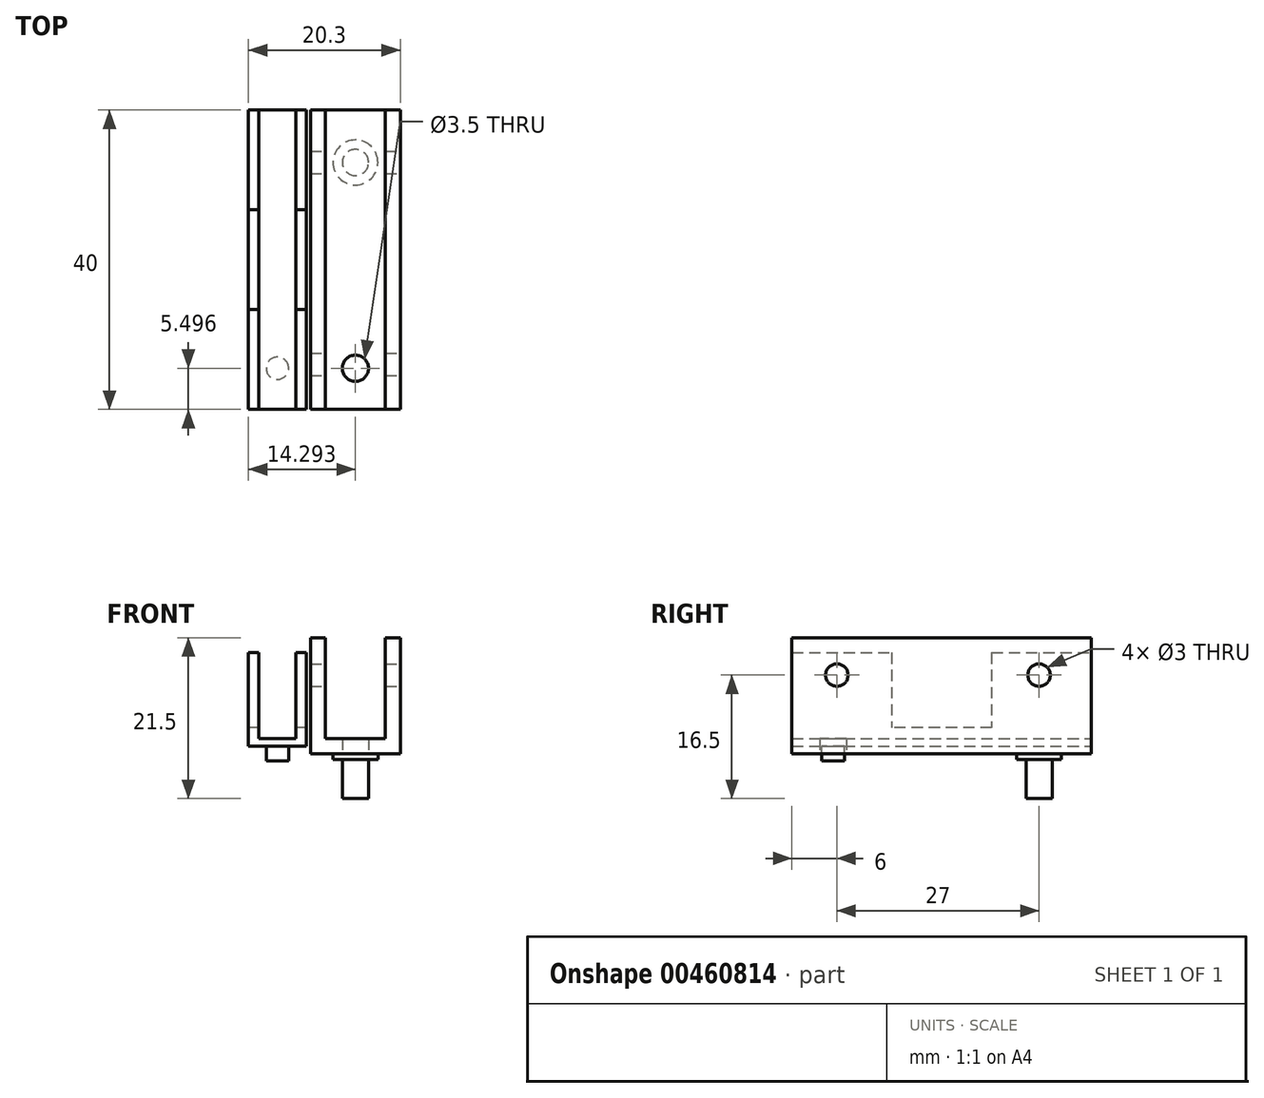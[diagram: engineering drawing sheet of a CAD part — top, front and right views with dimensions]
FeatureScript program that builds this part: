
annotation { "Feature Type Name" : "Feature", "Feature Type Description" : "" }
export const myFeature = defineFeature(function(context is Context, id is Id, definition is map)
    precondition{}
    {
        {
            var Q0;
            Q0=qCreatedBy(makeId("Front.planeOp"),FACE);
            var sketch = newSketch(context, id + "F0", { "sketchPlane" : qUnion([Q0])});
            skLineSegment(sketch, "E0", {"start": v(1.58, 13.5) * mm, "end": v(1.58, 0) * mm});
            skLineSegment(sketch, "E1", {"start": v(1.58, 0) * mm, "end": v(9.58, 0) * mm});
            skLineSegment(sketch, "E2", {"start": v(9.58, 0) * mm, "end": v(9.58, 13.5) * mm});
            skLineSegment(sketch, "E3", {"start": v(9.58, 13.5) * mm, "end": v(11.58, 13.5) * mm});
            skLineSegment(sketch, "E4", {"start": v(11.58, 13.5) * mm, "end": v(11.58, -2) * mm});
            skLineSegment(sketch, "E5", {"start": v(11.58, -2) * mm, "end": v(-0.42, -2) * mm});
            skLineSegment(sketch, "E6", {"start": v(-0.42, -2) * mm, "end": v(-0.42, 13.5) * mm});
            skLineSegment(sketch, "E7", {"start": v(-0.42, 13.5) * mm, "end": v(1.58, 13.5) * mm});
            skLineSegment(sketch, "E8", {"start": v(-4.18, 13.5) * mm, "end": v(14.97, 13.5) * mm, "construction": true});
            skSolve(sketch);
        }
        {
            var Q0;
            Q0=qCreatedBy(makeId("Front.planeOp"),FACE);
            var sketch = newSketch(context, id + "F1", { "sketchPlane" : qUnion([Q0])});
            skLineSegment(sketch, "E9", {"start": v(-7.32, 0) * mm, "end": v(-7.32, 11.5) * mm});
            skLineSegment(sketch, "E10", {"start": v(-7.32, 11.5) * mm, "end": v(-8.72, 11.5) * mm});
            skLineSegment(sketch, "E11", {"start": v(-8.72, 11.5) * mm, "end": v(-8.72, -1) * mm});
            skLineSegment(sketch, "E12", {"start": v(-8.72, -1) * mm, "end": v(-0.97, -1) * mm});
            skLineSegment(sketch, "E13", {"start": v(-0.97, -1) * mm, "end": v(-0.97, 11.5) * mm});
            skLineSegment(sketch, "E14", {"start": v(-0.97, 11.5) * mm, "end": v(-2.37, 11.5) * mm});
            skLineSegment(sketch, "E15", {"start": v(-2.37, 11.5) * mm, "end": v(-2.37, 0) * mm});
            skLineSegment(sketch, "E16", {"start": v(-2.37, 0) * mm, "end": v(-7.32, 0) * mm});
            skLineSegment(sketch, "E17", {"start": v(0, 11.5) * mm, "end": v(-10.25, 11.5) * mm, "construction": true});
            skPoint(sketch, "E17.startSnap0", {"position": v(-1.67, 11.5) * mm});
            skSolve(sketch);
        }
        {
            var Q0;
            Q0=makeQuery(id+"F0.imprint","IMPRINT",FACE,{"disambiguationData":[TD([[makeQuery(id+"F0.imprint","IMPRINT",EDGE,{"derivedFrom":sQuery(id+"F0.wireOp",EDGE,"E0")}),-1.0]])]});
            extrude(context, id + "F2", {"entities" : qUnion([Q0]), "depth" : 40 * mm});
        }
        {
            var Q0;
            Q0=makeQuery(id+"F1.imprint","IMPRINT",FACE,{"disambiguationData":[TD([[makeQuery(id+"F1.imprint","IMPRINT",EDGE,{"derivedFrom":sQuery(id+"F1.wireOp",EDGE,"E9")}),1.0]])]});
            extrude(context, id + "F3", {"entities" : qUnion([Q0]), "depth" : 40 * mm});
        }
        {
            var Q0;
            Q0=makeQuery(id+"F3.opExtrude","SWEPT_FACE",FACE,{"disambiguationData":[OSD([sQuery(id+"F1.wireOp",EDGE,"E11")])]});
            var sketch = newSketch(context, id + "F4", { "sketchPlane" : qUnion([Q0])});
            skLineSegment(sketch, "E18.bottom", {"start": v(13.33, 11.5) * mm, "end": v(26.67, 11.5) * mm});
            skLineSegment(sketch, "E18.top", {"start": v(13.33, 1.5) * mm, "end": v(26.67, 1.5) * mm});
            skLineSegment(sketch, "E18.left", {"start": v(13.33, 11.5) * mm, "end": v(13.33, 1.5) * mm});
            skLineSegment(sketch, "E18.right", {"start": v(26.67, 11.5) * mm, "end": v(26.67, 1.5) * mm});
            skSolve(sketch);
        }
        {
            var Q0;
            Q0 = qSketchRegion(id + "F4", true);
            extrude(context, id + "F5", {"entities" : qUnion([Q0]), "operationType" : NewBodyOperationType.REMOVE, "oppositeDirection" : true, "depth" : 8 * mm});
        }
        {
            var Q0;
            Q0=makeQuery(id+"F3.opExtrude","SWEPT_FACE",FACE,{"disambiguationData":[OSD([sQuery(id+"F1.wireOp",EDGE,"E12")])]});
            var sketch = newSketch(context, id + "F6", { "sketchPlane" : qUnion([Q0])});
            skLineSegment(sketch, "E19", {"start": v(-4.85, 40) * mm, "end": v(-4.85, 34.5) * mm, "construction": true});
            skCircle(sketch, "E20", {"center": v(-4.85, 34.5) * mm, "radius": 1.5 * mm});
            skSolve(sketch);
        }
        {
            var Q0;
            Q0 = qSketchRegion(id + "F6", true);
            extrude(context, id + "F7", {"entities" : qUnion([Q0]), "operationType" : NewBodyOperationType.ADD, "depth" : 2 * mm});
        }
        {
            var Q0;
            Q0=makeQuery(id+"F2.opExtrude","SWEPT_FACE",FACE,{"disambiguationData":[OSD([sQuery(id+"F0.wireOp",EDGE,"E5")])]});
            var sketch = newSketch(context, id + "F8", { "sketchPlane" : qUnion([Q0])});
            skLineSegment(sketch, "E21", {"start": v(5.58, 0) * mm, "end": v(5.58, 7) * mm});
            skCircle(sketch, "E22", {"center": v(5.58, 7) * mm, "radius": 1.75 * mm});
            skCircle(sketch, "E23", {"center": v(5.58, 7) * mm, "radius": 3 * mm});
            skLineSegment(sketch, "E24", {"start": v(5.58, 7) * mm, "end": v(11.58, 7) * mm, "construction": true});
            skLineSegment(sketch, "E25", {"start": v(5.58, 7) * mm, "end": v(5.58, 40) * mm, "construction": true});
            skLineSegment(sketch, "E26", {"start": v(11.58, 34.5) * mm, "end": v(5.58, 34.5) * mm, "construction": true});
            skSolve(sketch);
        }
        {
            var Q0;
            Q0 = qSketchRegion(id + "F8", true);
            extrude(context, id + "F9", {"entities" : qUnion([Q0]), "operationType" : NewBodyOperationType.ADD, "depth" : 0.75 * mm});
        }
        {
            var Q0;
            Q0=makeQuery(id+"F8.imprint","IMPRINT",FACE,{"disambiguationData":[TD([[makeQuery(id+"F8.imprint","IMPRINT",EDGE,{"derivedFrom":sQuery(id+"F8.wireOp",EDGE,"E22")}),1.0]])]});
            var Q1;
            Q1=sQuery(id+"F8.wireOp",EDGE,"E22");
            extrude(context, id + "F10", {"entities" : qUnion([Q0]), "operationType" : NewBodyOperationType.ADD, "surfaceEntities" : qUnion([Q1]), "depth" : 6 * mm});
        }
        {
            var Q0;
            Q0=makeQuery(id+"F2.opExtrude","SWEPT_FACE",FACE,{"disambiguationData":[OSD([sQuery(id+"F0.wireOp",EDGE,"E4")])]});
            var sketch = newSketch(context, id + "F11", { "sketchPlane" : qUnion([Q0])});
            skLineSegment(sketch, "E27", {"start": v(44.37, 8.5) * mm, "end": v(-84.46, 8.5) * mm, "construction": true});
            skLineSegment(sketch, "E28", {"start": v(0, 8.5) * mm, "end": v(-7, 8.5) * mm, "construction": true});
            skCircle(sketch, "E29", {"center": v(-7, 8.5) * mm, "radius": 1.5 * mm});
            skLineSegment(sketch, "E30", {"start": v(-40, 8.5) * mm, "end": v(-34, 8.5) * mm, "construction": true});
            skCircle(sketch, "E31", {"center": v(-34, 8.5) * mm, "radius": 1.5 * mm});
            skSolve(sketch);
        }
        {
            var Q0;
            Q0=makeQuery(id+"F11.imprint","IMPRINT",FACE,{"disambiguationData":[TD([[makeQuery(id+"F11.imprint","IMPRINT",EDGE,{"derivedFrom":sQuery(id+"F11.wireOp",EDGE,"E31")}),1.0]])]});
            var Q1;
            Q1=makeQuery(id+"F11.imprint","IMPRINT",FACE,{"disambiguationData":[TD([[makeQuery(id+"F11.imprint","IMPRINT",EDGE,{"derivedFrom":sQuery(id+"F11.wireOp",EDGE,"E29")}),1.0]])]});
            extrude(context, id + "F12", {"entities" : qUnion([Q0, Q1]), "operationType" : NewBodyOperationType.REMOVE, "oppositeDirection" : true, "depth" : 12 * mm});
        }
        {
            var Q0;
            Q0=makeQuery(id+"F8.imprint","IMPRINT",FACE,{"disambiguationData":[TD([[makeQuery(id+"F8.imprint","IMPRINT",EDGE,{"derivedFrom":sQuery(id+"F8.wireOp",EDGE,"E23")}),-1.0]])]});
            var sketch = newSketch(context, id + "F13", { "sketchPlane" : qUnion([Q0])});
            skCircle(sketch, "E32", {"center": v(5.57, 34.5) * mm, "radius": 1.75 * mm});
            skSolve(sketch);
        }
        {
            var Q0;
            Q0 = qSketchRegion(id + "F13", true);
            extrude(context, id + "F14", {"entities" : qUnion([Q0]), "operationType" : NewBodyOperationType.REMOVE, "oppositeDirection" : true, "depth" : 2 * mm});
        }
    });
